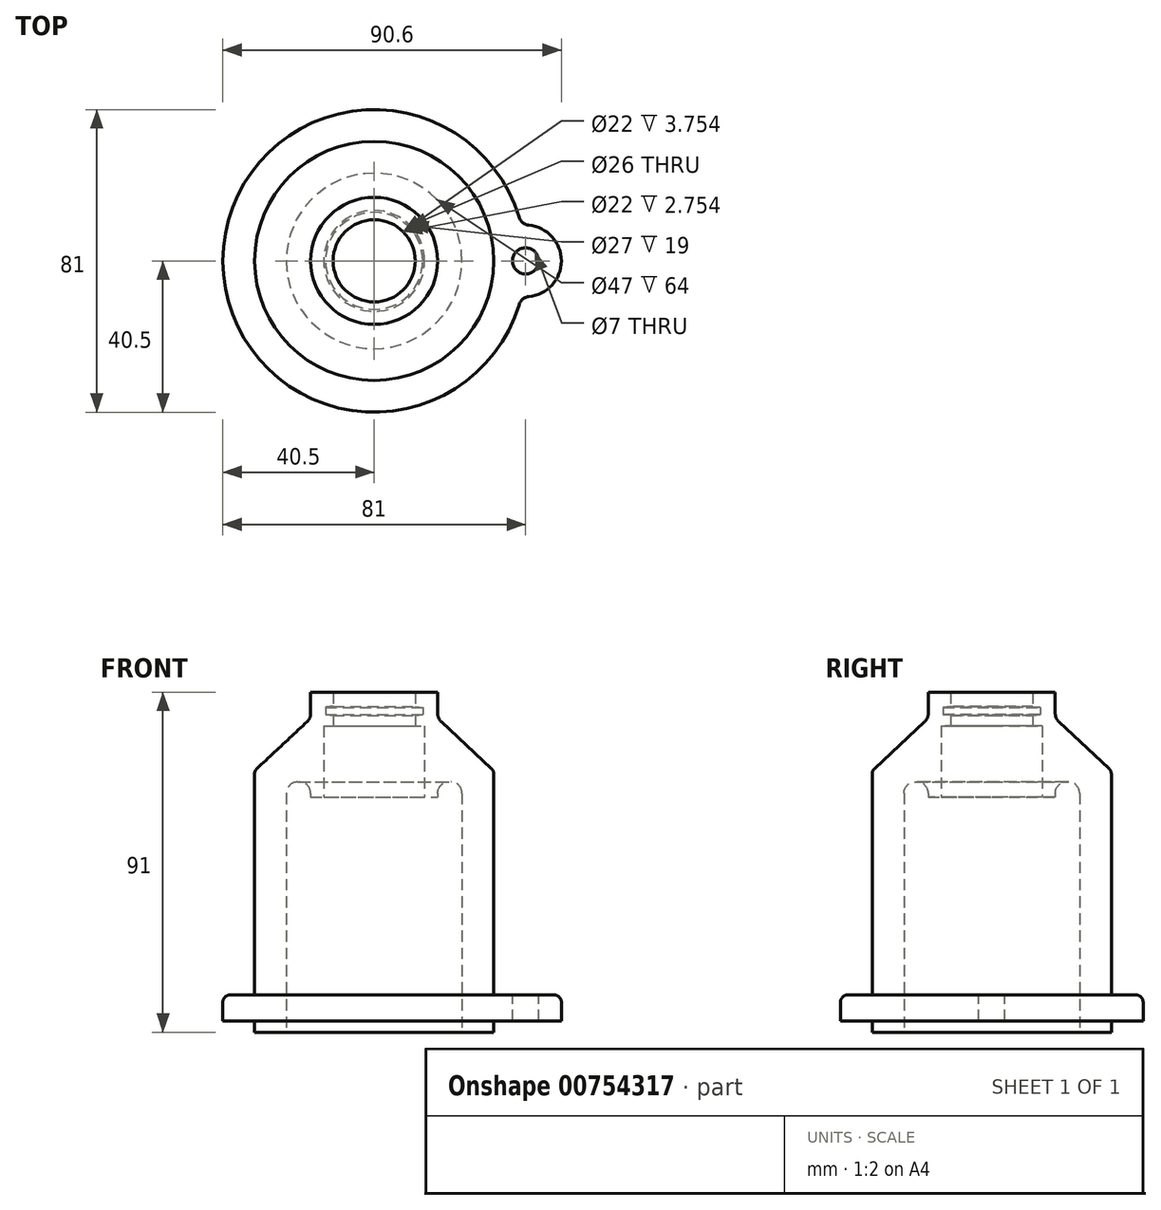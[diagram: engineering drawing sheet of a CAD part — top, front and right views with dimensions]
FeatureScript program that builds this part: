
annotation { "Feature Type Name" : "Feature", "Feature Type Description" : "" }
export const myFeature = defineFeature(function(context is Context, id is Id, definition is map)
    precondition{}
    {
        {
            var Q0;
            Q0=qCreatedBy(makeId("Front.planeOp"),FACE);
            var sketch = newSketch(context, id + "F0", { "sketchPlane" : qUnion([Q0])});
            skLineSegment(sketch, "E0", {"start": v(0, 0) * mm, "end": v(0, 86) * mm, "construction": true});
            skLineSegment(sketch, "E1", {"start": v(23.5, 0) * mm, "end": v(32, 0) * mm});
            skLineSegment(sketch, "E2", {"start": v(32, 0) * mm, "end": v(32, 3) * mm});
            skLineSegment(sketch, "E3", {"start": v(32, 3) * mm, "end": v(40.5, 3) * mm});
            skLineSegment(sketch, "E4", {"start": v(40.5, 3) * mm, "end": v(40.5, 10) * mm});
            skLineSegment(sketch, "E5", {"start": v(40.5, 10) * mm, "end": v(32, 10) * mm});
            skLineSegment(sketch, "E6", {"start": v(32, 10) * mm, "end": v(32, 70) * mm});
            skLineSegment(sketch, "E7", {"start": v(32, 70) * mm, "end": v(17, 84) * mm});
            skLineSegment(sketch, "E8", {"start": v(17, 84) * mm, "end": v(17, 91) * mm});
            skLineSegment(sketch, "E9", {"start": v(17, 91) * mm, "end": v(11, 91) * mm});
            skLineSegment(sketch, "E10", {"start": v(11, 91) * mm, "end": v(11, 87.25) * mm});
            skLineSegment(sketch, "E11", {"start": v(11, 82) * mm, "end": v(13.5, 82) * mm});
            skLineSegment(sketch, "E12", {"start": v(13.5, 82) * mm, "end": v(13.5, 63) * mm});
            skLineSegment(sketch, "E13", {"start": v(13.5, 63) * mm, "end": v(17, 63) * mm});
            skLineSegment(sketch, "E14", {"start": v(17, 63) * mm, "end": v(17, 64) * mm});
            skLineSegment(sketch, "E15", {"start": v(20, 67) * mm, "end": v(20.5, 67) * mm});
            skLineSegment(sketch, "E16", {"start": v(23.5, 64) * mm, "end": v(23.5, 0) * mm});
            skLineSegment(sketch, "E17", {"start": v(0, 86) * mm, "end": v(13, 86) * mm, "construction": true});
            skLineSegment(sketch, "E18", {"start": v(11, 87.25) * mm, "end": v(13, 87) * mm});
            skLineSegment(sketch, "E19", {"start": v(13, 87) * mm, "end": v(13, 86) * mm});
            skLineSegment(sketch, "E20.MirrorCS", {"start": v(11, 84.75) * mm, "end": v(13, 85) * mm});
            skLineSegment(sketch, "E21.MirrorCS", {"start": v(13, 85) * mm, "end": v(13, 86) * mm});
            skLineSegment(sketch, "E22.trimOffspring", {"start": v(11, 84.75) * mm, "end": v(11, 82) * mm});
            skPoint(sketch, "E23.visualSharp", {"position": v(17, 67) * mm});
            skArc(sketch, "E23.filletArc", {"start": v(20, 67) * mm, "mid": v(17.88, 66.12) * mm, "end": v(17, 64) * mm});
            skPoint(sketch, "E24.visualSharp", {"position": v(23.5, 67) * mm});
            skArc(sketch, "E24.filletArc", {"start": v(23.5, 64) * mm, "mid": v(22.62, 66.12) * mm, "end": v(20.5, 67) * mm});
            skSolve(sketch);
        }
        {
            var Q0;
            Q0 = qSketchRegion(id + "F0", true);
            var Q1;
            Q1=sQuery(id+"F0.wireOp",EDGE,"E0");
            revolve(context, id + "F1", {"surfaceOperationType" : NewSurfaceOperationType.NEW, "entities" : qUnion([Q0]), "axis" : qUnion([Q1]), "revolveType" : RevolveType.FULL});
        }
        {
            var Q0;
            Q0=makeQuery(id+"F1.opRevolve","SWEPT_FACE",FACE,{"disambiguationData":[OSD([sQuery(id+"F0.wireOp",EDGE,"E5")])]});
            var sketch = newSketch(context, id + "F2", { "sketchPlane" : qUnion([Q0])});
            skCircle(sketch, "E25.0", {"center": v(0, 0) * mm, "radius": 40.5 * mm, "construction": true});
            skCircle(sketch, "E26", {"center": v(40.5, 0) * mm, "radius": 9.6 * mm});
            skSolve(sketch);
        }
        {
            var Q0;
            Q0 = qSketchRegion(id + "F2", true);
            var Q1;
            Q1=makeQuery(id+"F1.opRevolve","SWEPT_FACE",FACE,{"disambiguationData":[OSD([sQuery(id+"F0.wireOp",EDGE,"E3")])]});
            extrude(context, id + "F3", {"entities" : qUnion([Q0]), "operationType" : NewBodyOperationType.ADD, "endBound" : BoundingType.UP_TO_SURFACE, "oppositeDirection" : true, "depth" : 7 * mm, "endBoundEntityFace" : qUnion([Q1]), "offsetDistance" : 25 * mm});
        }
        {
            var Q0;
            Q0=sQuery(id+"F2.wireOp",VERTEX,"E26.center");
            var Q1;
            Q1=makeQuery(id+"F1.opRevolve","SWEPT_BODY",BODY,{"disambiguationData":[OSD([sQuery(id+"F0.wireOp",EDGE,"E1"),sQuery(id+"F0.wireOp",EDGE,"E2"),sQuery(id+"F0.wireOp",EDGE,"E3"),sQuery(id+"F0.wireOp",EDGE,"E4"),sQuery(id+"F0.wireOp",EDGE,"E5"),sQuery(id+"F0.wireOp",EDGE,"E6"),sQuery(id+"F0.wireOp",EDGE,"E7"),sQuery(id+"F0.wireOp",EDGE,"E8"),sQuery(id+"F0.wireOp",EDGE,"E9"),sQuery(id+"F0.wireOp",EDGE,"E10"),sQuery(id+"F0.wireOp",EDGE,"E11"),sQuery(id+"F0.wireOp",EDGE,"E12"),sQuery(id+"F0.wireOp",EDGE,"E13"),sQuery(id+"F0.wireOp",EDGE,"E14"),sQuery(id+"F0.wireOp",EDGE,"E15"),sQuery(id+"F0.wireOp",EDGE,"E16"),sQuery(id+"F0.wireOp",EDGE,"E18"),sQuery(id+"F0.wireOp",EDGE,"E19"),sQuery(id+"F0.wireOp",EDGE,"E20.MirrorCS"),sQuery(id+"F0.wireOp",EDGE,"E21.MirrorCS"),sQuery(id+"F0.wireOp",EDGE,"E22.trimOffspring"),sQuery(id+"F0.wireOp",EDGE,"E23.filletArc"),sQuery(id+"F0.wireOp",EDGE,"E24.filletArc")])]});
            hole(context, id + "F4", {"style" : HoleStyle.SIMPLE, "endStyle" : HoleEndStyle.THROUGH, "holeDiameter" : 7 * mm, "majorDiameter" : 5 * mm, "tappedDepth" : 12 * mm, "tapClearance" : 3, "startFromSketch" : true, "locations" : qUnion([Q0]), "scope" : qUnion([Q1])});
        }
        {
            var Q0;
            Q0=makeQuery(id+"F3.boolean.opBoolean","INTERSECT",EDGE,{"disambiguationData":[OD(0.0)],"derivedFrom":[makeQuery(id+"F1.opRevolve","SWEPT_FACE",FACE,{"disambiguationData":[OSD([sQuery(id+"F0.wireOp",EDGE,"E4")])]}),makeQuery(id+"F3.opExtrude","SWEPT_FACE",FACE,{"disambiguationData":[OSD([sQuery(id+"F2.wireOp",EDGE,"E26")])]})]});
            var Q1;
            Q1=makeQuery(id+"F3.boolean.opBoolean","INTERSECT",EDGE,{"disambiguationData":[OD(1.0)],"derivedFrom":[makeQuery(id+"F1.opRevolve","SWEPT_FACE",FACE,{"disambiguationData":[OSD([sQuery(id+"F0.wireOp",EDGE,"E4")])]}),makeQuery(id+"F3.opExtrude","SWEPT_FACE",FACE,{"disambiguationData":[OSD([sQuery(id+"F2.wireOp",EDGE,"E26")])]})]});
            fillet(context, id + "F5", {"entities" : qUnion([Q0, Q1]), "radius" : 3 * mm, "tangentPropagation" : true, "allowEdgeOverflow" : false});
        }
        {
            var Q0;
            {var subQ0=sQuery(id+"F2.wireOp",EDGE,"E26");var subQ3=sQuery(id+"F0.wireOp",EDGE,"E4");var subQ4=makeQuery(id+"F1.opRevolve","SWEPT_FACE",FACE,{"disambiguationData":[OSD([subQ3])]});var subQ5=sQuery(id+"F0.wireOp",EDGE,"E5");var subQ7=makeQuery(id+"FFNpGQenNH4CeM2_1.1.F3.opExtrude","SWEPT_FACE",FACE,{"disambiguationData":[OSD([subQ0])]});Q0=makeQuery(id+"FFNpGQenNH4CeM2_1.2.F3.boolean.opBoolean","SPLIT",EDGE,{"disambiguationData":[TD([makeQuery(id+"FFNpGQenNH4CeM2_1.1.F5.opFillet","BLEND_FACE",FACE,{"disambiguationData":[OSD([subQ3,subQ0]),TDD([makeQuery(id+"FFNpGQenNH4CeM2_1.1.F3.boolean.opBoolean","INTERSECT",EDGE,{"disambiguationData":[OD(1.0)],"derivedFrom":[subQ4,subQ7]})])]})])],"derivedFrom":makeQuery(id+"FFNpGQenNH4CeM2_1.1.F3.boolean.opBoolean","SPLIT",EDGE,{"disambiguationData":[TD([makeQuery(id+"F5.opFillet","BLEND_FACE",FACE,{"disambiguationData":[OSD([subQ3,subQ0]),TDD([makeQuery(id+"F3.boolean.opBoolean","INTERSECT",EDGE,{"disambiguationData":[OD(1.0)],"derivedFrom":[subQ4,makeQuery(id+"F3.opExtrude","SWEPT_FACE",FACE,{"disambiguationData":[OSD([subQ0])]})]})])]})])],"derivedFrom":makeQuery(id+"F1.opRevolve","SWEPT_EDGE",EDGE,{"disambiguationData":[OSD([subQ3,subQ5])]})})});}
            var Q1;
            Q1=makeQuery(id+"F1.opRevolve","SWEPT_EDGE",EDGE,{"disambiguationData":[OSD([sQuery(id+"F0.wireOp",EDGE,"E6"),sQuery(id+"F0.wireOp",EDGE,"E7")])]});
            fillet(context, id + "F6", {"entities" : qUnion([Q0, Q1]), "radius" : 2 * mm, "tangentPropagation" : true, "allowEdgeOverflow" : false});
        }
        {
            var Q0;
            Q0=makeQuery(id+"F1.opRevolve","SWEPT_EDGE",EDGE,{"disambiguationData":[OSD([sQuery(id+"F0.wireOp",EDGE,"E7"),sQuery(id+"F0.wireOp",EDGE,"E8")])]});
            var Q1;
            Q1=makeQuery(id+"F1.opRevolve","SWEPT_EDGE",EDGE,{"disambiguationData":[OSD([sQuery(id+"F0.wireOp",EDGE,"E5"),sQuery(id+"F0.wireOp",EDGE,"E6")])]});
            fillet(context, id + "F7", {"entities" : qUnion([Q0, Q1]), "radius" : 3 * mm, "tangentPropagation" : true, "allowEdgeOverflow" : false});
        }
    });
